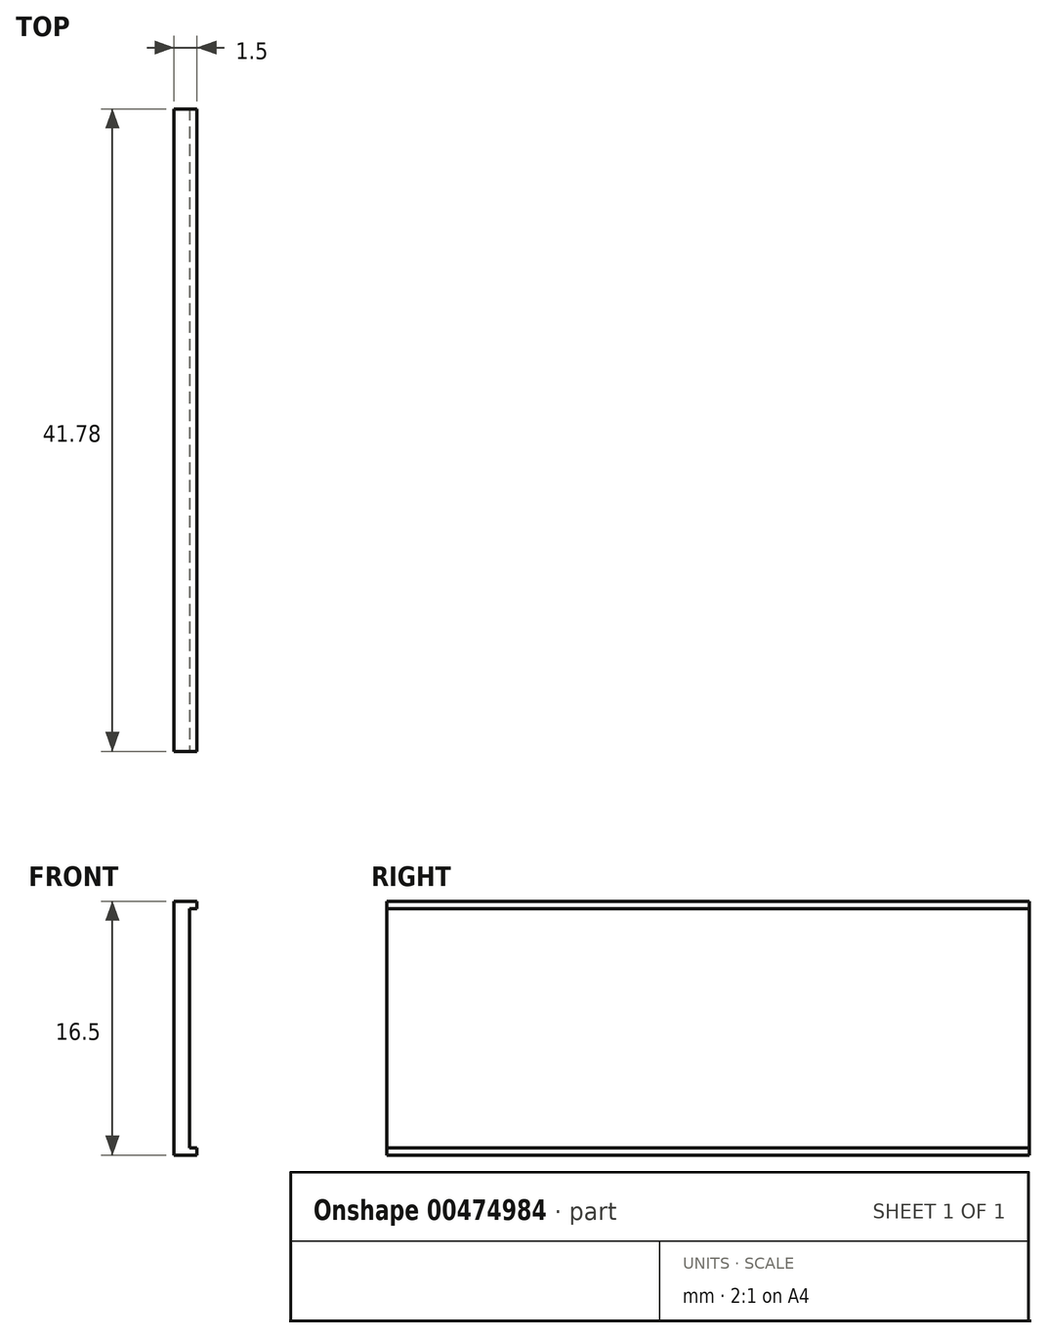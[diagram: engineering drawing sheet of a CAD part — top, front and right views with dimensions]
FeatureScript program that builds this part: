
annotation { "Feature Type Name" : "Feature", "Feature Type Description" : "" }
export const myFeature = defineFeature(function(context is Context, id is Id, definition is map)
    precondition{}
    {
        {
            var Q0;
            Q0=qCreatedBy(makeId("Right.planeOp"),FACE);
            var sketch = newSketch(context, id + "F0", { "sketchPlane" : qUnion([Q0])});
            skLineSegment(sketch, "E0.bottom", {"start": v(-20.9, 8.25) * mm, "end": v(20.9, 8.25) * mm});
            skLineSegment(sketch, "E0.top", {"start": v(-20.9, -8.25) * mm, "end": v(20.9, -8.25) * mm});
            skLineSegment(sketch, "E0.left", {"start": v(-20.9, 8.25) * mm, "end": v(-20.9, -8.25) * mm});
            skLineSegment(sketch, "E0.right", {"start": v(20.9, 8.25) * mm, "end": v(20.9, -8.25) * mm});
            skPoint(sketch, "E0.middle", {"position": v(0, 0) * mm});
            skLineSegment(sketch, "E1.top", {"start": v(-20.9, -7.77) * mm, "end": v(20.9, -7.77) * mm});
            skLineSegment(sketch, "E1.left", {"start": v(-20.9, -8.25) * mm, "end": v(-20.9, -7.77) * mm});
            skLineSegment(sketch, "E1.right", {"start": v(20.9, -8.25) * mm, "end": v(20.9, -7.77) * mm});
            skLineSegment(sketch, "E2.MirrorCS", {"start": v(-20.9, 7.77) * mm, "end": v(20.9, 7.77) * mm});
            skSolve(sketch);
        }
        {
            var Q0;
            Q0=makeQuery(id+"F0.imprint","IMPRINT",FACE,{"disambiguationData":[TD([[makeQuery(id+"F0.imprint","IMPRINT",EDGE,{"derivedFrom":sQuery(id+"F0.wireOp",EDGE,"E0.top")}),1.0]])]});
            extrude(context, id + "F1", {"entities" : qUnion([Q0]), "depth" : 1.5 * mm});
        }
        {
            var Q0;
            Q0=qSketchRegion(id+"F0",true);
            extrude(context, id + "F2", {"entities" : qUnion([Q0]), "operationType" : NewBodyOperationType.ADD, "depth" : 1 * mm});
        }
        {
            var Q0;
            {var subQ0=sQuery(id+"F0.wireOp",EDGE,"E0.bottom");Q0=makeQuery(id+"F0.imprint","IMPRINT",FACE,{"disambiguationData":[TD([[makeQuery(id+"F0.imprint","IMPRINT",EDGE,{"derivedFrom":subQ0}),-1.0]])]});}
            extrude(context, id + "F3", {"entities" : qUnion([Q0]), "operationType" : NewBodyOperationType.ADD, "depth" : 1.5 * mm});
        }
    });
